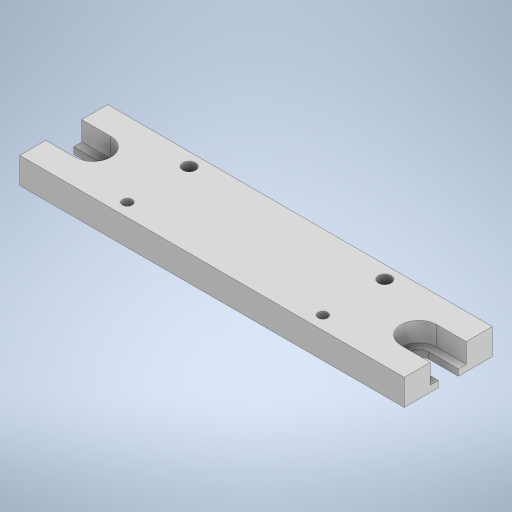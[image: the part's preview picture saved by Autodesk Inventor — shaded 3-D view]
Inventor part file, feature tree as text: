
AUTODESK INVENTOR PART (.ipt)
format: ipt  version: 2023 (Build 270158000, 158)  size: 458,752 bytes
history: native  units: mm
features: extrude x3, sketch x1
ambient origin geometry x8: Origin, YZ Plane, XZ Plane, XY Plane, X Axis, Y Axis, Z Axis, Center Point
bodies: Body1 (feature_tree)
feature tree (4):
  sketch  "Sketch1"  dims[d162=60.0mm d163=60.0mm d165=100.0mm d173=90.0mm d183=11.0mm d184=11.0mm d185=6.15mm d186=6.15mm d187=3.95mm d188=2.98mm d189=3.95mm d190=2.98mm d202=9.0mm d203=9.0mm d204=9.0mm d212=19.0mm d213=19.0mm d214=27.0mm d215=4.0mm d216=4.0mm d217=13.5mm d218=30.0mm d219=30.0mm d220=8.0mm d221=0.0mm d222=2.0mm d223=0.0mm d224=2.0mm d225=0.0mm]
  extrude  "Extrusion13"  Depth=11.0mm
  extrude  "Extrusion14"  Depth=11.0mm
  extrude  "Extrusion15"  Depth=6.15mm
